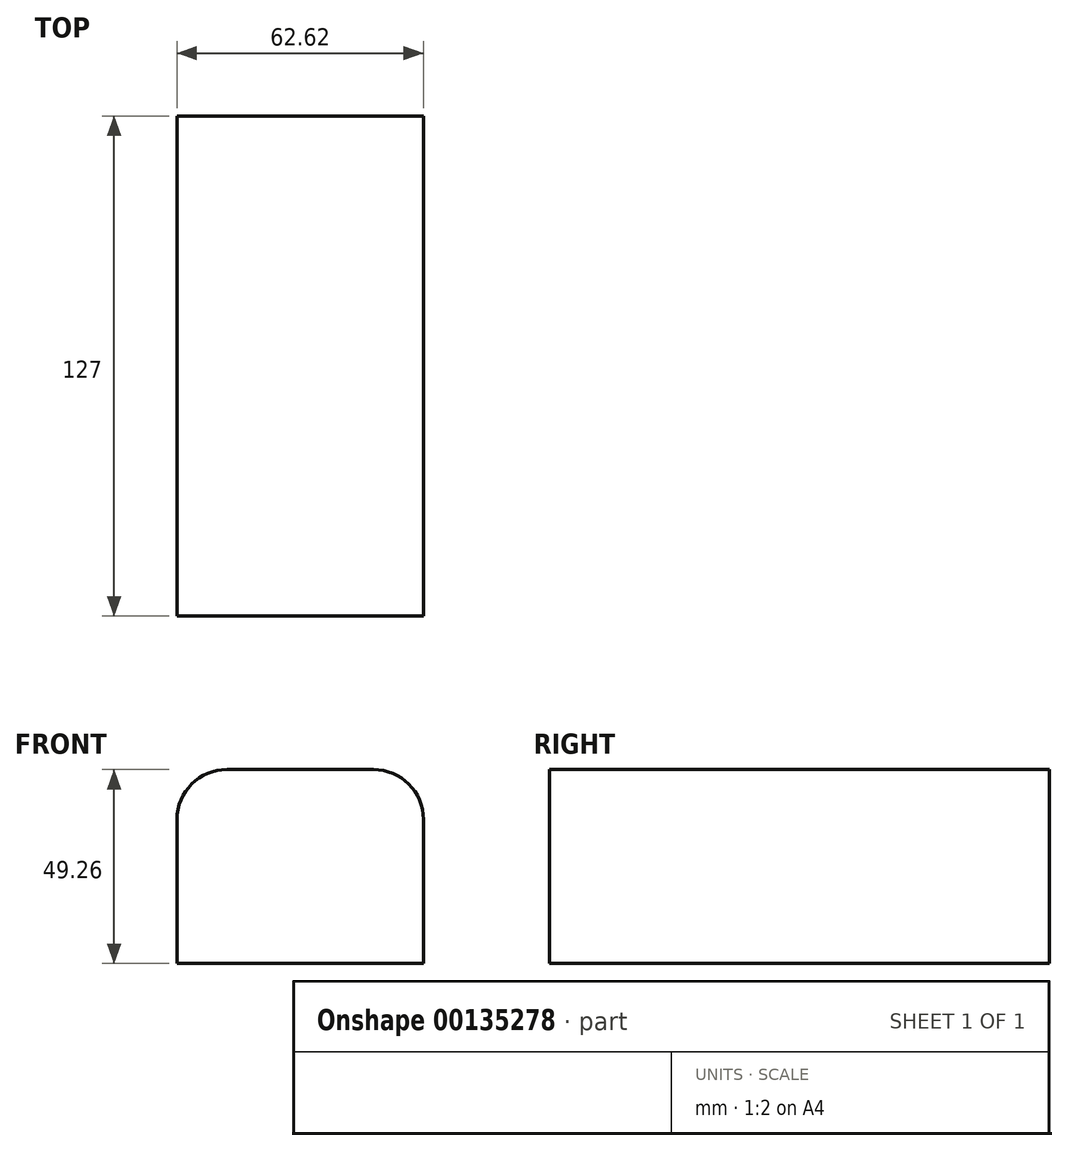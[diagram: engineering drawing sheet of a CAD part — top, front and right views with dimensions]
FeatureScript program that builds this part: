
annotation { "Feature Type Name" : "Feature", "Feature Type Description" : "" }
export const myFeature = defineFeature(function(context is Context, id is Id, definition is map)
    precondition{}
    {
        {
            var Q0;
            Q0=qCreatedBy(makeId("Front.planeOp"),FACE);
            var sketch = newSketch(context, id + "F0", { "sketchPlane" : qUnion([Q0])});
            skLineSegment(sketch, "E0.bottom", {"start": v(0, 0) * mm, "end": v(62.62, 0) * mm});
            skLineSegment(sketch, "E0.top", {"start": v(0, -49.26) * mm, "end": v(62.62, -49.26) * mm});
            skLineSegment(sketch, "E0.left", {"start": v(0, 0) * mm, "end": v(0, -49.26) * mm});
            skLineSegment(sketch, "E0.right", {"start": v(62.62, 0) * mm, "end": v(62.62, -49.26) * mm});
            skSolve(sketch);
        }
        {
            var Q0;
            Q0=makeQuery(id+"F0.imprint","IMPRINT",FACE,{"disambiguationData":[TD([[makeQuery(id+"F0.imprint","IMPRINT",EDGE,{"derivedFrom":sQuery(id+"F0.wireOp",EDGE,"E0.bottom")}),-1.0]])]});
            extrude(context, id + "F1", {"entities" : qUnion([Q0]), "depth" : 127 * mm});
        }
        {
            var Q0;
            Q0=makeQuery(id+"F1.opExtrude","SWEPT_EDGE",EDGE,{"disambiguationData":[OSD([sQuery(id+"F0.wireOp",EDGE,"E0.bottom"),sQuery(id+"F0.wireOp",EDGE,"E0.right")])]});
            var Q1;
            Q1=makeQuery(id+"F1.opExtrude","SWEPT_EDGE",EDGE,{"disambiguationData":[OSD([sQuery(id+"F0.wireOp",EDGE,"E0.bottom"),sQuery(id+"F0.wireOp",EDGE,"E0.left")])]});
            fillet(context, id + "F2", {"entities" : qUnion([Q0, Q1]), "radius" : 12.7 * mm, "tangentPropagation" : true, "allowEdgeOverflow" : false});
        }
    });
